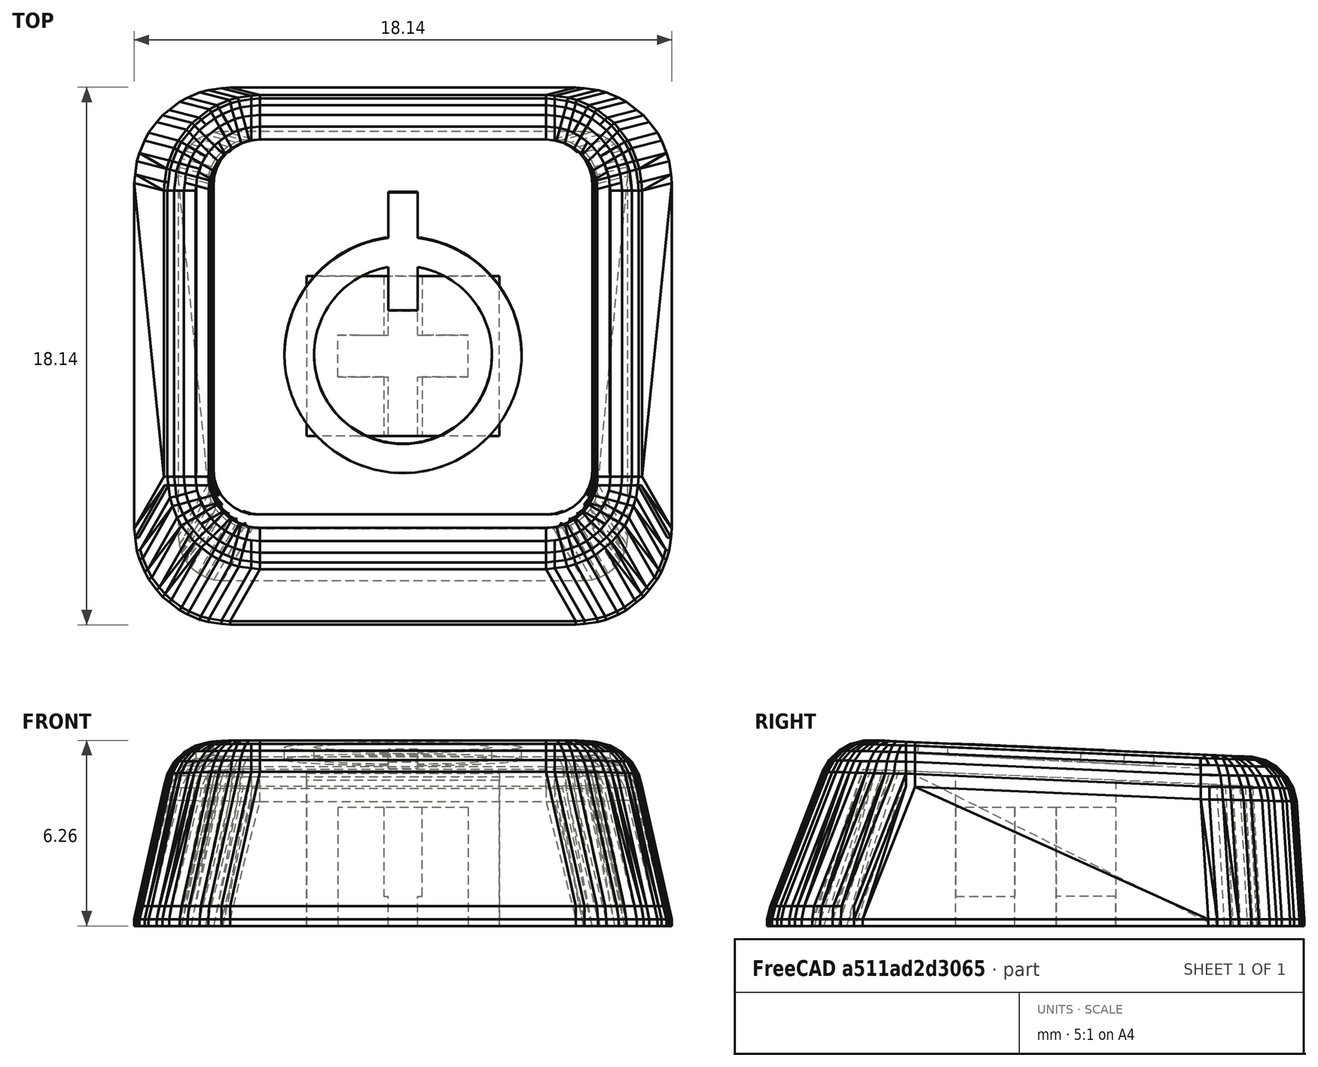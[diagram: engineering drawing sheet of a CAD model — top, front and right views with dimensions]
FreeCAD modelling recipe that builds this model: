
FCSTD DOCUMENT  (FreeCAD 0.18R16131 (Git))
Label: power
License: All rights reserved
LicenseURL: http://en.wikipedia.org/wiki/All_rights_reserved
objects: Part::Box×5, Part::MultiFuse×2, Part::Cylinder×2, Part::Cut×2, Part::Feature×1
note: 12 computed .brp shape members not serialized (recipe doc carries the construction recipe); baked Part::Feature solids carry a one-line shape summary decoded from their .brp

FEATURE [Part::Feature] Solid
  shape: bbox 18.13 x 18.13 x 6.262 mm, 1259 faces (baked)
FEATURE [Part::Box] Box  label="Cube"
  AttacherType = Attacher::AttachEngine3D
  Height = 1
  Length = 1
  Placement = pos=(0.5,-2.7,0) rot=(0,0,1;0rad)
  Width = 2
FEATURE [Part::Box] Box001  label="Cube001"
  AttacherType = Attacher::AttachEngine3D
  Height = 1
  Length = 1
  Placement = pos=(-1.5,0.7,0) rot=(0,0,1;0rad)
  Width = 2
FEATURE [Part::Box] Box002  label="Cube002"
  AttacherType = Attacher::AttachEngine3D
  Height = 1
  Length = 1
  Placement = pos=(-1.5,-2.7,0) rot=(0,0,1;0rad)
  Width = 2
FEATURE [Part::Box] Box003  label="Cube003"
  AttacherType = Attacher::AttachEngine3D
  Height = 1
  Length = 1
  Placement = pos=(0.5,0.7,0) rot=(0,0,1;0rad)
  Width = 2
FEATURE [Part::MultiFuse] Fusion
  Shapes = -> [Solid,Box002,Box001,Box,Box003]
FEATURE [Part::Cylinder] Cylinder
  Angle = 360
  AttacherType = Attacher::AttachEngine3D
  Height = 0.5
  Placement = pos=(0,1,10) rot=(0,0,1;0rad)
  Radius = 4
FEATURE [Part::Cylinder] Cylinder001
  Angle = 360
  AttacherType = Attacher::AttachEngine3D
  Height = 0.5
  Placement = pos=(0,1,10) rot=(0,0,1;0rad)
  Radius = 3
FEATURE [Part::Box] Box004  label="Cube004"
  AttacherType = Attacher::AttachEngine3D
  Height = 0.5
  Length = 1
  Placement = pos=(-0.5,2,10) rot=(0,0,1;0rad)
  Width = 4
FEATURE [Part::Cut] Cut
  Base = -> Cylinder
  Placement = pos=(0,-0.5,0) rot=(0,0,1;0rad)
  Tool = -> Cylinder001
FEATURE [Part::MultiFuse] Fusion001
  Placement = pos=(0,-1,-4.35) rot=(1,0,0;-0.05236rad)
  Shapes = -> [Cut,Box004]
FEATURE [Part::Cut] Cut001
  Base = -> Fusion
  Tool = -> Fusion001
